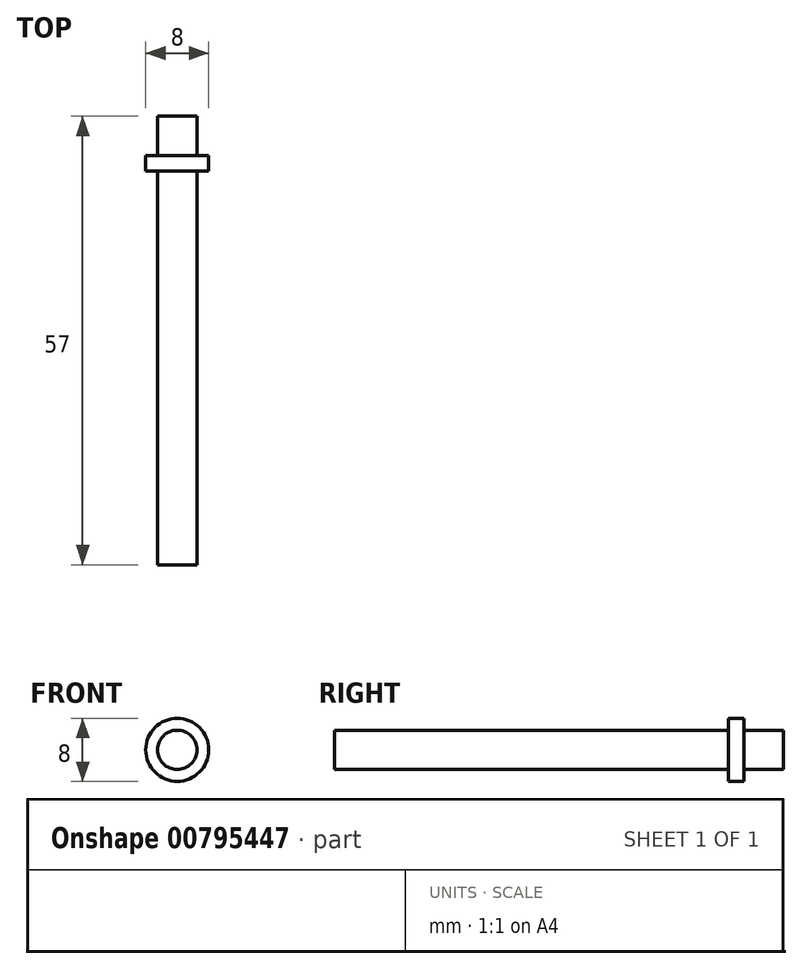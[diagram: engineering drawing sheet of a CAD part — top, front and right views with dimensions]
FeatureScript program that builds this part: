
annotation { "Feature Type Name" : "Feature", "Feature Type Description" : "" }
export const myFeature = defineFeature(function(context is Context, id is Id, definition is map)
    precondition{}
    {
        {
            var Q0;
            Q0=qCreatedBy(makeId("Front.planeOp"),FACE);
            var sketch = newSketch(context, id + "F0", { "sketchPlane" : qUnion([Q0])});
            skCircle(sketch, "E0", {"center": v(0, 0) * mm, "radius": 2.5 * mm});
            skSolve(sketch);
        }
        {
            var Q0;
            Q0=qSketchRegion(id+"F0",true);
            extrude(context, id + "F1", {"entities" : qUnion([Q0]), "depth" : 5 * mm, "offsetDistance" : 25 * mm});
        }
        {
            var Q0;
            Q0=makeQuery(id+"F1.opExtrude","CAP_FACE",FACE,{"disambiguationData":[OSD([sQuery(id+"F0.wireOp",EDGE,"E0")])],"isStart":false});
            var sketch = newSketch(context, id + "F2", { "sketchPlane" : qUnion([Q0])});
            skCircle(sketch, "E1", {"center": v(0, 0) * mm, "radius": 4 * mm});
            skSolve(sketch);
        }
        {
            var Q0;
            Q0=qSketchRegion(id+"F2",true);
            extrude(context, id + "F3", {"entities" : qUnion([Q0]), "operationType" : NewBodyOperationType.ADD, "depth" : 2 * mm, "offsetDistance" : 25 * mm});
        }
        {
            var Q0;
            Q0=makeQuery(id+"F3.opExtrude","CAP_FACE",FACE,{"disambiguationData":[OSD([sQuery(id+"F2.wireOp",EDGE,"E1")])],"isStart":false});
            var sketch = newSketch(context, id + "F4", { "sketchPlane" : qUnion([Q0])});
            skCircle(sketch, "E2", {"center": v(0, 0) * mm, "radius": 2.5 * mm});
            skSolve(sketch);
        }
        {
            var Q0;
            Q0=makeQuery(id+"F4.imprint","IMPRINT",FACE,{"disambiguationData":[TD([[makeQuery(id+"F4.imprint","IMPRINT",EDGE,{"derivedFrom":sQuery(id+"F4.wireOp",EDGE,"E2")}),1.0]])]});
            extrude(context, id + "F5", {"entities" : qUnion([Q0]), "operationType" : NewBodyOperationType.ADD, "depth" : 25 * mm, "offsetDistance" : 25 * mm});
        }
        {
            var Q0;
            Q0=makeQuery(id+"F5.opExtrude","CAP_FACE",FACE,{"disambiguationData":[OSD([sQuery(id+"F4.wireOp",EDGE,"E2")])],"isStart":false});
            extrude(context, id + "F6", {"entities" : qUnion([Q0]), "operationType" : NewBodyOperationType.ADD, "depth" : 25 * mm, "offsetDistance" : 25 * mm});
        }
    });
